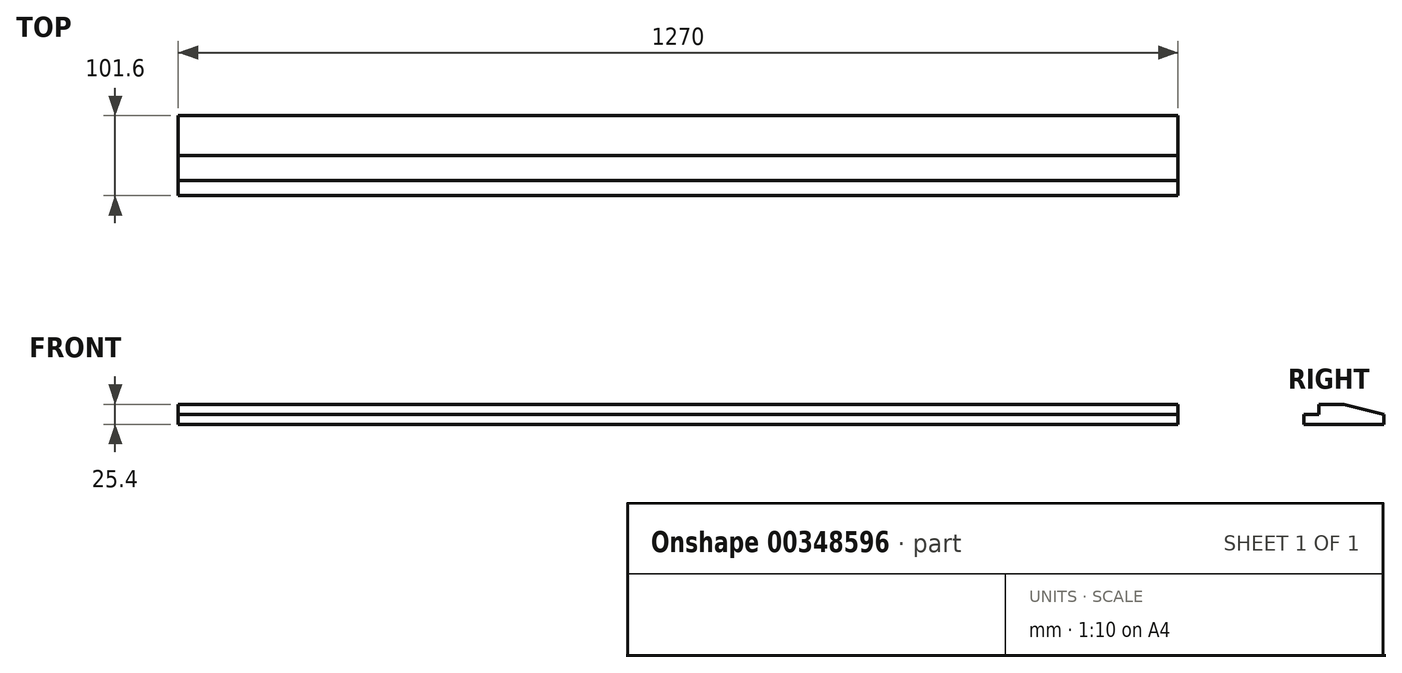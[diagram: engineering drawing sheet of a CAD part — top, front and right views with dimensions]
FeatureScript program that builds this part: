
annotation { "Feature Type Name" : "Feature", "Feature Type Description" : "" }
export const myFeature = defineFeature(function(context is Context, id is Id, definition is map)
    precondition{}
    {
        {
            var Q0;
            Q0=qCreatedBy(makeId("Top.planeOp"),FACE);
            var sketch = newSketch(context, id + "F0", { "sketchPlane" : qUnion([Q0])});
            skLineSegment(sketch, "E0.bottom", {"start": v(-256.04, 59.7) * mm, "end": v(1013.96, 59.7) * mm});
            skLineSegment(sketch, "E0.top", {"start": v(-256.04, -41.9) * mm, "end": v(1013.96, -41.9) * mm});
            skLineSegment(sketch, "E0.left", {"start": v(-256.04, 59.7) * mm, "end": v(-256.04, -41.9) * mm});
            skLineSegment(sketch, "E0.right", {"start": v(1013.96, 59.7) * mm, "end": v(1013.96, -41.9) * mm});
            skLineSegment(sketch, "E1", {"start": v(-256.04, -22.84) * mm, "end": v(1013.96, -22.84) * mm});
            skSolve(sketch);
        }
        {
            var Q0;
            {var subQ0=sQuery(id+"F0.wireOp",EDGE,"E0.bottom");Q0=makeQuery(id+"F0.imprint","IMPRINT",FACE,{"disambiguationData":[TD([[makeQuery(id+"F0.imprint","IMPRINT",EDGE,{"derivedFrom":subQ0}),-1.0]])]});}
            extrude(context, id + "F1", {"entities" : qUnion([Q0]), "depth" : 12.7 * mm});
        }
        {
            var Q0;
            Q0 = qSketchRegion(id + "F0", true);
            var Q1;
            Q1=makeQuery(id+"F1.opExtrude","CAP_FACE",FACE,{"disambiguationData":[OSD([sQuery(id+"F0.wireOp",EDGE,"E0.bottom"),sQuery(id+"F0.wireOp",EDGE,"E0.left"),sQuery(id+"F0.wireOp",EDGE,"E0.right"),sQuery(id+"F0.wireOp",EDGE,"E1")])],"isStart":false});
            extrude(context, id + "F2", {"entities" : qUnion([Q0, Q1]), "operationType" : NewBodyOperationType.ADD, "depth" : 12.7 * mm});
        }
        {
            var Q0;
            {var subQ0=sQuery(id+"F0.wireOp",EDGE,"E0.bottom");Q0=makeQuery(id+"F2.opExtrude","CAP_EDGE",EDGE,{"disambiguationData":[OSD([subQ0]),TDD([makeQuery(id+"F1.opExtrude","CAP_EDGE",EDGE,{"disambiguationData":[OSD([subQ0])],"isStart":false})])],"isStart":false});}
            chamfer(context, id + "F3", {"entities" : qUnion([Q0]), "chamferType" : ChamferType.TWO_OFFSETS, "width1" : 12.7 * mm, "oppositeDirection" : false, "width2" : 50.8 * mm, "tangentPropagation" : true});
        }
    });
